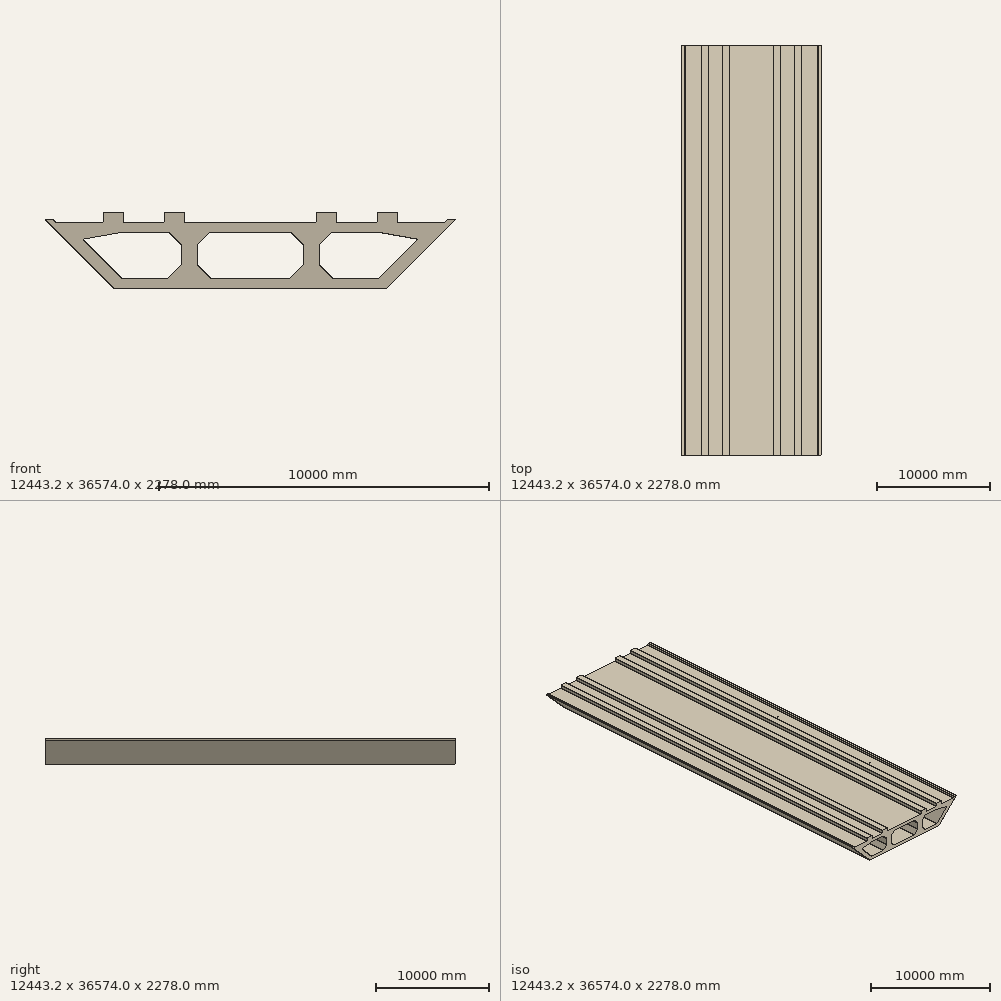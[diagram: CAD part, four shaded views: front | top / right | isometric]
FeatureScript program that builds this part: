
annotation { "Feature Type Name" : "Feature", "Feature Type Description" : "" }
export const myFeature = defineFeature(function(context is Context, id is Id, definition is map)
    precondition{}
    {
        {
            var Q0;
            Q0=qCreatedBy(makeId("Front.planeOp"),FACE);
            var sketch = newSketch(context, id + "F0", { "sketchPlane" : qUnion([Q0])});
            skLineSegment(sketch, "E0", {"start": v(76.45, 1978) * mm, "end": v(2000, 1978) * mm});
            skLineSegment(sketch, "E1", {"start": v(76.45, 1978) * mm, "end": v(-2000, 1978) * mm});
            skPoint(sketch, "E2.orphan", {"position": v(-4046.68, 0) * mm});
            skLineSegment(sketch, "E3", {"start": v(0, 0) * mm, "end": v(-4142, 0) * mm});
            skLineSegment(sketch, "E4", {"start": v(0, 0) * mm, "end": v(4142, 0) * mm});
            skLineSegment(sketch, "E5", {"start": v(-4142, 0) * mm, "end": v(-6120, 1978) * mm});
            skLineSegment(sketch, "E6", {"start": v(4142, 0) * mm, "end": v(6120, 1978) * mm});
            skLineSegment(sketch, "E7", {"start": v(6120, 1978) * mm, "end": v(6221.6, 2079.6) * mm});
            skLineSegment(sketch, "E8", {"start": v(6221.6, 2079.6) * mm, "end": v(6008.6, 2079.6) * mm});
            skLineSegment(sketch, "E9", {"start": v(6008.6, 2079.6) * mm, "end": v(5907, 1978) * mm});
            skLineSegment(sketch, "E10", {"start": v(-6120, 1978) * mm, "end": v(-6221.6, 2079.6) * mm});
            skLineSegment(sketch, "E11", {"start": v(-6221.6, 2079.6) * mm, "end": v(-6008.6, 2079.6) * mm});
            skLineSegment(sketch, "E12", {"start": v(-6008.6, 2079.6) * mm, "end": v(-5907, 1978) * mm});
            skLineSegment(sketch, "E13.bottom", {"start": v(-1212.6, 1689) * mm, "end": v(1212.6, 1689) * mm});
            skLineSegment(sketch, "E13.top", {"start": v(-1212.6, 289) * mm, "end": v(1212.6, 289) * mm});
            skLineSegment(sketch, "E13.left", {"start": v(-1601.5, 1300.1) * mm, "end": v(-1601.5, 677.9) * mm});
            skLineSegment(sketch, "E13.right", {"start": v(1601.5, 1300.1) * mm, "end": v(1601.5, 677.9) * mm});
            skLineSegment(sketch, "E14", {"start": v(0, 0) * mm, "end": v(0, 2929.04) * mm, "construction": true});
            skLineSegment(sketch, "E15", {"start": v(-1601.5, 1300.1) * mm, "end": v(-1212.6, 1689) * mm});
            skLineSegment(sketch, "E16", {"start": v(1212.6, 1689) * mm, "end": v(1601.5, 1300.1) * mm});
            skLineSegment(sketch, "E17", {"start": v(-1601.5, 677.9) * mm, "end": v(-1212.6, 289) * mm});
            skLineSegment(sketch, "E18", {"start": v(1601.5, 677.9) * mm, "end": v(1212.6, 289) * mm});
            skPoint(sketch, "E19.orphan", {"position": v(1601.5, 289) * mm});
            skLineSegment(sketch, "E20.bottom", {"start": v(-2490.4, 1689) * mm, "end": v(-3901.5, 1689) * mm});
            skLineSegment(sketch, "E20.top", {"start": v(-2490.4, 289) * mm, "end": v(-3901.5, 289) * mm});
            skLineSegment(sketch, "E20.left", {"start": v(-2101.5, 1689) * mm, "end": v(-2101.5, 677.9) * mm});
            skLineSegment(sketch, "E21.bottom", {"start": v(2490.4, 1689) * mm, "end": v(3901.5, 1689) * mm});
            skLineSegment(sketch, "E21.top", {"start": v(2490.4, 289) * mm, "end": v(3901.5, 289) * mm});
            skLineSegment(sketch, "E21.left", {"start": v(2101.5, 1300.1) * mm, "end": v(2101.5, 677.9) * mm});
            skLineSegment(sketch, "E22", {"start": v(-4450, 1978) * mm, "end": v(-4450, 2278) * mm});
            skLineSegment(sketch, "E23", {"start": v(-4450, 2278) * mm, "end": v(-3850, 2278) * mm});
            skLineSegment(sketch, "E24", {"start": v(-3850, 2278) * mm, "end": v(-3850, 1978) * mm});
            skLineSegment(sketch, "E25", {"start": v(-2600, 1978) * mm, "end": v(-2600, 2278) * mm});
            skLineSegment(sketch, "E26", {"start": v(-2600, 2278) * mm, "end": v(-2000, 2278) * mm});
            skLineSegment(sketch, "E27", {"start": v(-2000, 2278) * mm, "end": v(-2000, 1978) * mm});
            skLineSegment(sketch, "E28.trimOffspring", {"start": v(-4450, 1978) * mm, "end": v(-5907, 1978) * mm});
            skLineSegment(sketch, "E29.trimOffspring", {"start": v(-2600, 1978) * mm, "end": v(-3850, 1978) * mm});
            skLineSegment(sketch, "E30", {"start": v(2000, 1978) * mm, "end": v(2000, 2278) * mm});
            skLineSegment(sketch, "E31", {"start": v(2000, 2278) * mm, "end": v(2600, 2278) * mm});
            skLineSegment(sketch, "E32", {"start": v(2600, 2278) * mm, "end": v(2600, 1978) * mm});
            skLineSegment(sketch, "E33", {"start": v(3850, 1978) * mm, "end": v(3850, 2278) * mm});
            skPoint(sketch, "E33.endSnap0", {"position": v(2300, 2278) * mm});
            skLineSegment(sketch, "E34", {"start": v(3850, 2278) * mm, "end": v(4450, 2278) * mm});
            skLineSegment(sketch, "E35", {"start": v(4450, 2278) * mm, "end": v(4450, 1978) * mm});
            skLineSegment(sketch, "E36.trimOffspring", {"start": v(4450, 1978) * mm, "end": v(5907, 1978) * mm});
            skLineSegment(sketch, "E37.trimOffspring", {"start": v(2600, 1978) * mm, "end": v(3850, 1978) * mm});
            skLineSegment(sketch, "E38", {"start": v(4150, 2278) * mm, "end": v(4150, 2496.72) * mm, "construction": true});
            skLineSegment(sketch, "E39", {"start": v(2300, 2278) * mm, "end": v(2300, 2592.02) * mm, "construction": true});
            skLineSegment(sketch, "E40", {"start": v(-2300, 2278) * mm, "end": v(-2300, 2659.76) * mm, "construction": true});
            skLineSegment(sketch, "E41", {"start": v(-4150, 2278) * mm, "end": v(-4150, 2688.6) * mm, "construction": true});
            skLineSegment(sketch, "E42", {"start": v(2101.5, 1300.1) * mm, "end": v(2490.4, 1689) * mm});
            skLineSegment(sketch, "E43", {"start": v(2101.5, 677.9) * mm, "end": v(2490.4, 289) * mm});
            skLineSegment(sketch, "E44", {"start": v(-2490.4, 1689) * mm, "end": v(-2101.5, 1300.1) * mm});
            skLineSegment(sketch, "E45", {"start": v(-2101.5, 677.9) * mm, "end": v(-2490.4, 289) * mm});
            skPoint(sketch, "E46.orphan", {"position": v(2101.5, 1689) * mm});
            skLineSegment(sketch, "E47", {"start": v(3901.5, 289) * mm, "end": v(5091.65, 1479.15) * mm});
            skLineSegment(sketch, "E48", {"start": v(3901.5, 1689) * mm, "end": v(5091.65, 1479.15) * mm});
            skLineSegment(sketch, "E49", {"start": v(-3901.5, 289) * mm, "end": v(-5091.65, 1479.15) * mm});
            skLineSegment(sketch, "E50", {"start": v(-3901.5, 1689) * mm, "end": v(-5091.65, 1479.15) * mm});
            skSolve(sketch);
        }
        {
            var Q0;
            Q0=makeQuery(id+"F0.imprint","IMPRINT",FACE,{"disambiguationData":[TD([[makeQuery(id+"F0.imprint","IMPRINT",EDGE,{"derivedFrom":sQuery(id+"F0.wireOp",EDGE,"E0")}),-1.0]])]});
            extrude(context, id + "F1", {"entities" : qUnion([Q0]), "depth" : 36574 * mm, "offsetDistance" : 25 * mm});
        }
        {
            var Q0;
            Q0=makeQuery(id+"F1.opExtrude","SWEPT_FACE",FACE,{"disambiguationData":[OSD([sQuery(id+"F0.wireOp",EDGE,"E36.trimOffspring")])]});
            var sketch = newSketch(context, id + "F2", { "sketchPlane" : qUnion([Q0])});
            skLineSegment(sketch, "E51", {"start": v(5075, -36574) * mm, "end": v(5075, 0) * mm, "construction": true});
            skCircle(sketch, "E52", {"center": v(5075, -36374) * mm, "radius": 10 * mm});
            skCircle(sketch, "E53", {"center": v(5075, -35374) * mm, "radius": 10 * mm});
            skCircle(sketch, "E54", {"center": v(5240, -36304) * mm, "radius": 10 * mm});
            skCircle(sketch, "E55", {"center": v(5240, -36444) * mm, "radius": 9.8 * mm});
            skCircle(sketch, "E56.0.1.1", {"center": v(5240, -35304) * mm, "radius": 10 * mm});
            skCircle(sketch, "E56.0.1.2", {"center": v(5240, -35444) * mm, "radius": 9.8 * mm});
            skCircle(sketch, "E56.0.2.0", {"center": v(5075, -34374) * mm, "radius": 10 * mm});
            skCircle(sketch, "E56.0.2.1", {"center": v(5240, -34304) * mm, "radius": 10 * mm});
            skCircle(sketch, "E56.0.2.2", {"center": v(5240, -34444) * mm, "radius": 9.8 * mm});
            skCircle(sketch, "E56.0.3.0", {"center": v(5075, -33374) * mm, "radius": 10 * mm});
            skCircle(sketch, "E56.0.3.1", {"center": v(5240, -33304) * mm, "radius": 10 * mm});
            skCircle(sketch, "E56.0.3.2", {"center": v(5240, -33444) * mm, "radius": 9.8 * mm});
            skCircle(sketch, "E56.0.4.0", {"center": v(5075, -32374) * mm, "radius": 10 * mm});
            skCircle(sketch, "E56.0.4.1", {"center": v(5240, -32304) * mm, "radius": 10 * mm});
            skCircle(sketch, "E56.0.4.2", {"center": v(5240, -32444) * mm, "radius": 9.8 * mm});
            skCircle(sketch, "E56.0.5.0", {"center": v(5075, -31374) * mm, "radius": 10 * mm});
            skCircle(sketch, "E56.0.5.1", {"center": v(5240, -31304) * mm, "radius": 10 * mm});
            skCircle(sketch, "E56.0.5.2", {"center": v(5240, -31444) * mm, "radius": 9.8 * mm});
            skCircle(sketch, "E56.0.6.0", {"center": v(5075, -30374) * mm, "radius": 10 * mm});
            skCircle(sketch, "E56.0.6.1", {"center": v(5240, -30304) * mm, "radius": 10 * mm});
            skCircle(sketch, "E56.0.6.2", {"center": v(5240, -30444) * mm, "radius": 9.8 * mm});
            skCircle(sketch, "E56.0.7.0", {"center": v(5075, -29374) * mm, "radius": 10 * mm});
            skCircle(sketch, "E56.0.7.1", {"center": v(5240, -29304) * mm, "radius": 10 * mm});
            skCircle(sketch, "E56.0.7.2", {"center": v(5240, -29444) * mm, "radius": 9.8 * mm});
            skCircle(sketch, "E56.0.8.0", {"center": v(5075, -28374) * mm, "radius": 10 * mm});
            skCircle(sketch, "E56.0.8.1", {"center": v(5240, -28304) * mm, "radius": 10 * mm});
            skCircle(sketch, "E56.0.8.2", {"center": v(5240, -28444) * mm, "radius": 9.8 * mm});
            skCircle(sketch, "E56.0.9.0", {"center": v(5075, -27374) * mm, "radius": 10 * mm});
            skCircle(sketch, "E56.0.9.1", {"center": v(5240, -27304) * mm, "radius": 10 * mm});
            skCircle(sketch, "E56.0.9.2", {"center": v(5240, -27444) * mm, "radius": 9.8 * mm});
            skCircle(sketch, "E56.0.10.0", {"center": v(5075, -26374) * mm, "radius": 10 * mm});
            skCircle(sketch, "E56.0.10.1", {"center": v(5240, -26304) * mm, "radius": 10 * mm});
            skCircle(sketch, "E56.0.10.2", {"center": v(5240, -26444) * mm, "radius": 9.8 * mm});
            skCircle(sketch, "E56.0.11.0", {"center": v(5075, -25374) * mm, "radius": 10 * mm});
            skCircle(sketch, "E56.0.11.1", {"center": v(5240, -25304) * mm, "radius": 10 * mm});
            skCircle(sketch, "E56.0.11.2", {"center": v(5240, -25444) * mm, "radius": 9.8 * mm});
            skCircle(sketch, "E56.0.12.0", {"center": v(5075, -24374) * mm, "radius": 10 * mm});
            skCircle(sketch, "E56.0.12.1", {"center": v(5240, -24304) * mm, "radius": 10 * mm});
            skCircle(sketch, "E56.0.12.2", {"center": v(5240, -24444) * mm, "radius": 9.8 * mm});
            skCircle(sketch, "E56.0.13.0", {"center": v(5075, -23374) * mm, "radius": 10 * mm});
            skCircle(sketch, "E56.0.13.1", {"center": v(5240, -23304) * mm, "radius": 10 * mm});
            skCircle(sketch, "E56.0.13.2", {"center": v(5240, -23444) * mm, "radius": 9.8 * mm});
            skCircle(sketch, "E56.0.14.0", {"center": v(5075, -22374) * mm, "radius": 10 * mm});
            skCircle(sketch, "E56.0.14.1", {"center": v(5240, -22304) * mm, "radius": 10 * mm});
            skCircle(sketch, "E56.0.14.2", {"center": v(5240, -22444) * mm, "radius": 9.8 * mm});
            skCircle(sketch, "E56.0.15.0", {"center": v(5075, -21374) * mm, "radius": 10 * mm});
            skCircle(sketch, "E56.0.15.1", {"center": v(5240, -21304) * mm, "radius": 10 * mm});
            skCircle(sketch, "E56.0.15.2", {"center": v(5240, -21444) * mm, "radius": 9.8 * mm});
            skCircle(sketch, "E56.0.16.0", {"center": v(5075, -20374) * mm, "radius": 10 * mm});
            skCircle(sketch, "E56.0.16.1", {"center": v(5240, -20304) * mm, "radius": 10 * mm});
            skCircle(sketch, "E56.0.16.2", {"center": v(5240, -20444) * mm, "radius": 9.8 * mm});
            skCircle(sketch, "E56.0.17.0", {"center": v(5075, -19374) * mm, "radius": 10 * mm});
            skCircle(sketch, "E56.0.17.1", {"center": v(5240, -19304) * mm, "radius": 10 * mm});
            skCircle(sketch, "E56.0.17.2", {"center": v(5240, -19444) * mm, "radius": 9.8 * mm});
            skCircle(sketch, "E56.0.18.0", {"center": v(5075, -18374) * mm, "radius": 10 * mm});
            skCircle(sketch, "E56.0.18.1", {"center": v(5240, -18304) * mm, "radius": 10 * mm});
            skCircle(sketch, "E56.0.18.2", {"center": v(5240, -18444) * mm, "radius": 9.8 * mm});
            skCircle(sketch, "E56.0.19.0", {"center": v(5075, -17374) * mm, "radius": 10 * mm});
            skCircle(sketch, "E56.0.19.1", {"center": v(5240, -17304) * mm, "radius": 10 * mm});
            skCircle(sketch, "E56.0.19.2", {"center": v(5240, -17444) * mm, "radius": 9.8 * mm});
            skCircle(sketch, "E56.0.20.0", {"center": v(5075, -16374) * mm, "radius": 10 * mm});
            skCircle(sketch, "E56.0.20.1", {"center": v(5240, -16304) * mm, "radius": 10 * mm});
            skCircle(sketch, "E56.0.20.2", {"center": v(5240, -16444) * mm, "radius": 9.8 * mm});
            skCircle(sketch, "E56.0.21.0", {"center": v(5075, -15374) * mm, "radius": 10 * mm});
            skCircle(sketch, "E56.0.21.1", {"center": v(5240, -15304) * mm, "radius": 10 * mm});
            skCircle(sketch, "E56.0.21.2", {"center": v(5240, -15444) * mm, "radius": 9.8 * mm});
            skCircle(sketch, "E56.0.22.0", {"center": v(5075, -14374) * mm, "radius": 10 * mm});
            skCircle(sketch, "E56.0.22.1", {"center": v(5240, -14304) * mm, "radius": 10 * mm});
            skCircle(sketch, "E56.0.22.2", {"center": v(5240, -14444) * mm, "radius": 9.8 * mm});
            skCircle(sketch, "E56.0.23.0", {"center": v(5075, -13374) * mm, "radius": 10 * mm});
            skCircle(sketch, "E56.0.23.1", {"center": v(5240, -13304) * mm, "radius": 10 * mm});
            skCircle(sketch, "E56.0.23.2", {"center": v(5240, -13444) * mm, "radius": 9.8 * mm});
            skCircle(sketch, "E56.0.24.0", {"center": v(5075, -12374) * mm, "radius": 10 * mm});
            skCircle(sketch, "E56.0.24.1", {"center": v(5240, -12304) * mm, "radius": 10 * mm});
            skCircle(sketch, "E56.0.24.2", {"center": v(5240, -12444) * mm, "radius": 9.8 * mm});
            skCircle(sketch, "E56.0.25.0", {"center": v(5075, -11374) * mm, "radius": 10 * mm});
            skCircle(sketch, "E56.0.25.1", {"center": v(5240, -11304) * mm, "radius": 10 * mm});
            skCircle(sketch, "E56.0.25.2", {"center": v(5240, -11444) * mm, "radius": 9.8 * mm});
            skCircle(sketch, "E56.0.26.0", {"center": v(5075, -10374) * mm, "radius": 10 * mm});
            skCircle(sketch, "E56.0.26.1", {"center": v(5240, -10304) * mm, "radius": 10 * mm});
            skCircle(sketch, "E56.0.26.2", {"center": v(5240, -10444) * mm, "radius": 9.8 * mm});
            skCircle(sketch, "E56.0.27.0", {"center": v(5075, -9374) * mm, "radius": 10 * mm});
            skCircle(sketch, "E56.0.27.1", {"center": v(5240, -9304) * mm, "radius": 10 * mm});
            skCircle(sketch, "E56.0.27.2", {"center": v(5240, -9444) * mm, "radius": 9.8 * mm});
            skCircle(sketch, "E56.0.28.0", {"center": v(5075, -8374) * mm, "radius": 10 * mm});
            skCircle(sketch, "E56.0.28.1", {"center": v(5240, -8304) * mm, "radius": 10 * mm});
            skCircle(sketch, "E56.0.28.2", {"center": v(5240, -8444) * mm, "radius": 9.8 * mm});
            skCircle(sketch, "E56.0.29.0", {"center": v(5075, -7374) * mm, "radius": 10 * mm});
            skCircle(sketch, "E56.0.29.1", {"center": v(5240, -7304) * mm, "radius": 10 * mm});
            skCircle(sketch, "E56.0.29.2", {"center": v(5240, -7444) * mm, "radius": 9.8 * mm});
            skLineSegment(sketch, "E56.direction1", {"start": v(5075, -36374) * mm, "end": v(5075, -36374) * mm});
            skLineSegment(sketch, "E56.direction2", {"start": v(5075, -36374) * mm, "end": v(5075, -35374) * mm, "construction": true});
            skSolve(sketch);
        }
        {
            var Q0;
            Q0 = qSketchRegion(id + "F2", true);
            extrude(context, id + "F3", {"entities" : qUnion([Q0]), "operationType" : NewBodyOperationType.REMOVE, "oppositeDirection" : true, "depth" : 100 * mm, "offsetDistance" : 25 * mm});
        }
    });
